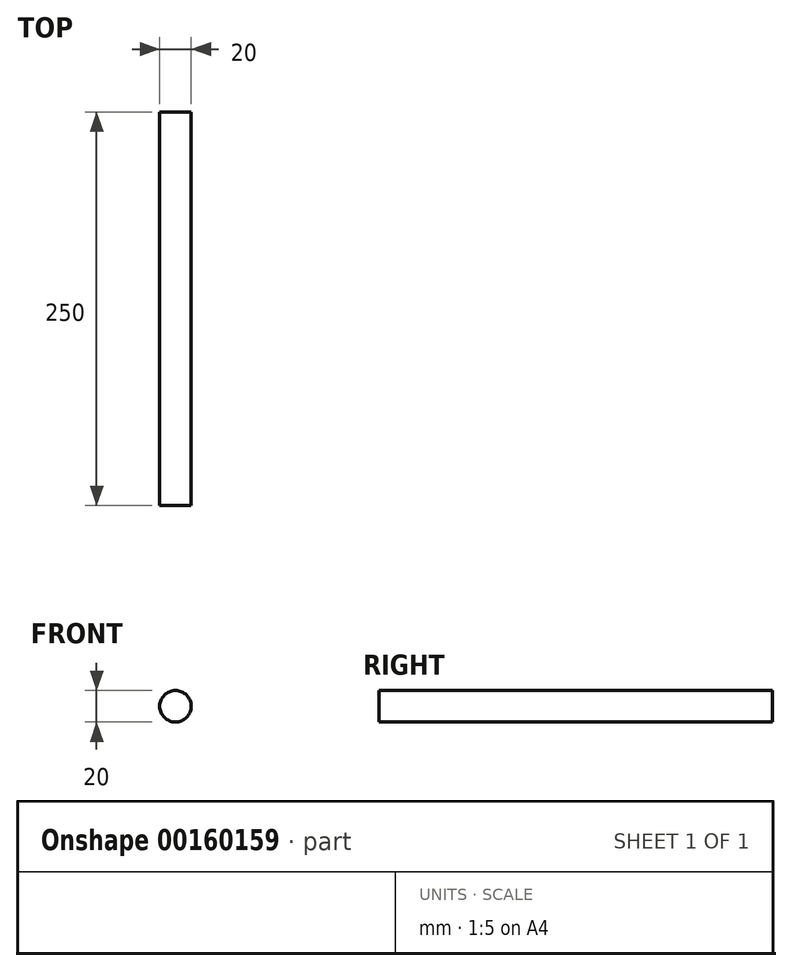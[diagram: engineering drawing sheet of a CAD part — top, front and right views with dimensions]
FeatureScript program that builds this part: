
annotation { "Feature Type Name" : "Feature", "Feature Type Description" : "" }
export const myFeature = defineFeature(function(context is Context, id is Id, definition is map)
    precondition{}
    {
        {
            var Q0;
            Q0=qCreatedBy(makeId("Front.planeOp"),FACE);
            var sketch = newSketch(context, id + "F0", { "sketchPlane" : qUnion([Q0])});
            skCircle(sketch, "E0", {"center": v(0, 0) * mm, "radius": 10 * mm});
            skSolve(sketch);
        }
        {
            var Q0;
            Q0=makeQuery(id+"F0.imprint","IMPRINT",FACE,{"disambiguationData":[TD([[makeQuery(id+"F0.imprint","IMPRINT",EDGE,{"derivedFrom":sQuery(id+"F0.wireOp",EDGE,"E0")}),-1.0]])]});
            var Q1;
            Q1=makeQuery(id+"F0.imprint","IMPRINT",FACE,{"disambiguationData":[TD([[makeQuery(id+"F0.imprint","IMPRINT",EDGE,{"derivedFrom":sQuery(id+"F0.wireOp",EDGE,"E0")}),1.0]])]});
            extrude(context, id + "F1", {"entities" : qUnion([Q0, Q1]), "depth" : 250 * mm});
        }
    });
